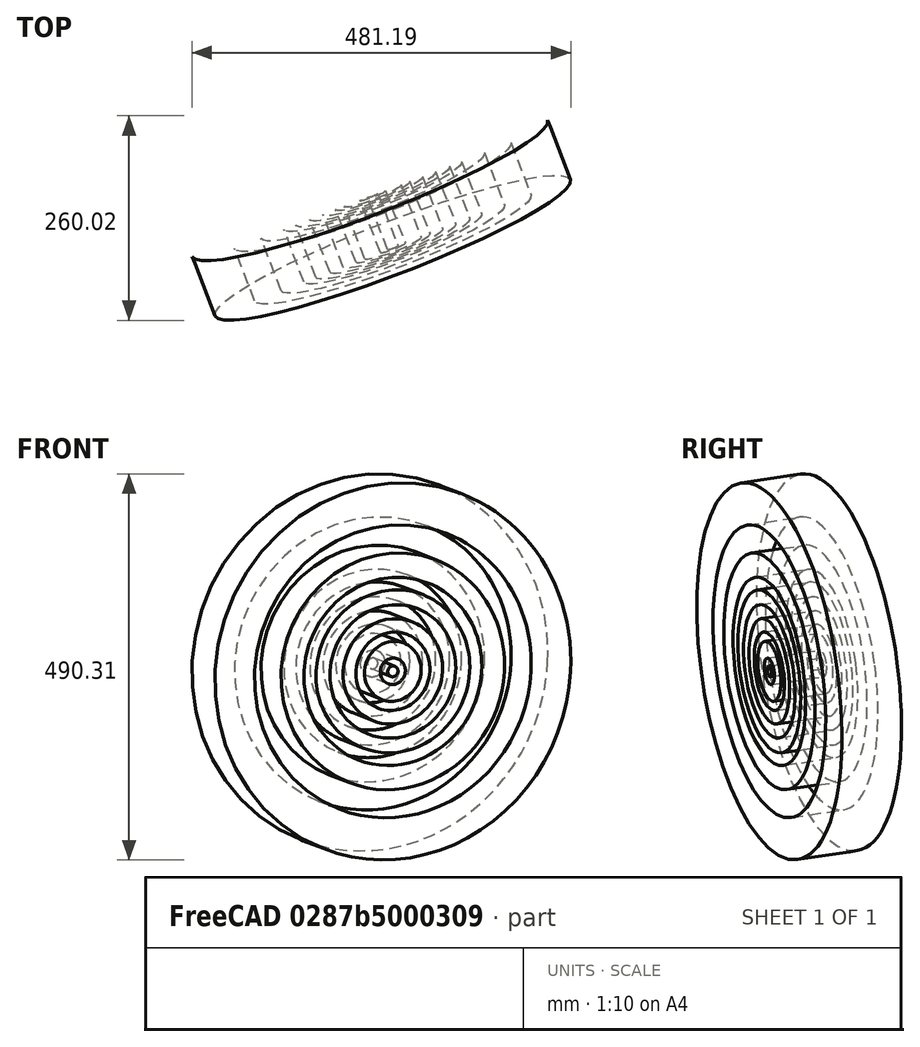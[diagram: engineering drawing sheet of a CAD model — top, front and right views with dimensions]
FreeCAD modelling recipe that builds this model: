
FCSTD DOCUMENT  (FreeCAD 0.20R25997 (Git))
Label: wirefilter_bullseye_example
License: All rights reserved
LicenseURL: http://en.wikipedia.org/wiki/All_rights_reserved
objects: Part::FeaturePython×2, PartDesign::Pad×2, Sketcher::SketchObject×1, PartDesign::Body×1
note: 8 computed .brp shape members not serialized (recipe doc carries the construction recipe); baked Part::Feature solids carry a one-line shape summary decoded from their .brp

FEATURE [Sketcher::SketchObject] Sketch
  AttachmentOffset = pos=(0,0,0) rot=(0.352249,0.933626,-0.065286;0.391935rad)
  FullyConstrained = false
  MapMode = 5
  Placement = pos=(0,0,0) rot=(0.971145,0.179991,0.156464;1.73935rad)
  sketch-geometry (15):
    g0: Circle CenterX=0 CenterY=0 CenterZ=0 NormalX=0 NormalY=0 NormalZ=1 AngleXU=0 Radius=6.93157
    g1: Circle CenterX=0 CenterY=0 CenterZ=0 NormalX=0 NormalY=0 NormalZ=1 AngleXU=0 Radius=17.0215
    g2: Circle CenterX=0 CenterY=0 CenterZ=0 NormalX=0 NormalY=0 NormalZ=1 AngleXU=0 Radius=38.5048
    g3: Circle CenterX=0 CenterY=0 CenterZ=0 NormalX=0 NormalY=0 NormalZ=1 AngleXU=0 Radius=50.3417
    g4: Circle CenterX=0 CenterY=0 CenterZ=0 NormalX=0 NormalY=0 NormalZ=1 AngleXU=0 Radius=67.6191
    g5: Circle CenterX=0 CenterY=0 CenterZ=0 NormalX=0 NormalY=0 NormalZ=1 AngleXU=0 Radius=85.57
    g6: Circle CenterX=0 CenterY=0 CenterZ=0 NormalX=0 NormalY=0 NormalZ=1 AngleXU=0 Radius=104.602
    g7: Circle CenterX=0 CenterY=0 CenterZ=0 NormalX=0 NormalY=0 NormalZ=1 AngleXU=0 Radius=120.851
    g8: Circle CenterX=0 CenterY=0 CenterZ=0 NormalX=0 NormalY=0 NormalZ=1 AngleXU=0 Radius=151.869
    g9: Circle CenterX=0 CenterY=0 CenterZ=0 NormalX=0 NormalY=0 NormalZ=1 AngleXU=0 Radius=187.882
    g10: Circle CenterX=0 CenterY=0 CenterZ=0 NormalX=0 NormalY=0 NormalZ=1 AngleXU=0 Radius=241.809
    g11: LineSegment StartX=-153.303 StartY=49.7272 StartZ=0 EndX=171.131 EndY=49.7272 EndZ=0
    g12: LineSegment StartX=171.131 StartY=49.7272 StartZ=0 EndX=171.131 EndY=-77.5486 EndZ=0
    g13: LineSegment StartX=171.131 StartY=-77.5486 StartZ=0 EndX=-153.303 EndY=-77.5486 EndZ=0
    g14: LineSegment StartX=-153.303 StartY=-77.5486 StartZ=0 EndX=-153.303 EndY=49.7272 EndZ=0
  constraints (20):
    c: Coincident(g0,g-1)
    c: Coincident(g1,g0)
    c: Coincident(g2,g0)
    c: Coincident(g3,g0)
    c: Coincident(g4,g0)
    c: Coincident(g5,g0)
    c: Coincident(g6,g0)
    c: Coincident(g7,g0)
    c: Coincident(g8,g0)
    c: Coincident(g9,g0)
    c: Coincident(g10,g0)
    c: Coincident(g11,g12)
    c: Coincident(g12,g13)
    c: Coincident(g13,g14)
    c: Coincident(g14,g11)
    c: Horizontal(g11)
    c: Horizontal(g13)
    c: Vertical(g12)
    c: Vertical(g14)
    c: PointOnObject(g12,g9)
FEATURE [Part::FeaturePython] WireFilter  # WARN: FeaturePython — macro-defined, semantics opaque (R4)
  AttacherType = Attacher::AttachEngine3D
  ClaimChildren = true
  FaceMaker = 1
  FixNormal = false
  FollowSource = true
  Normal = (-0.35488,0.924495,0.139173)
  OffsetFill = false
  OffsetIntersection = false
  OffsetJoin = 0
  OffsetOpenResult = false
  Scale = (1,1,1)
  SelectEdges = false
  Source = -> Sketch [Edge11,Edge10,Edge9,Edge8,Edge7,Edge6,Edge5,Edge4,Edge3,Edge2,Edge1]
  UseDefault = false
  UseSelected = true
  UseSelectedEdges = false
  Version = 0.2021.10.20
  WireOrder = [1,2,3,4,5,6,7,8,9,10,11,0]
FEATURE [Part::FeaturePython] WireFilter001  # WARN: FeaturePython — macro-defined, semantics opaque (R4)
  AttacherType = Attacher::AttachEngine3D
  ClaimChildren = true
  FaceMaker = 0
  FixNormal = false
  FollowSource = true
  Normal = (-0.35488,0.924495,0.139173)
  OffsetFill = false
  OffsetIntersection = false
  OffsetJoin = 0
  OffsetOpenResult = false
  Scale = (1,1,1)
  SelectEdges = false
  Source = -> Sketch
  UseDefault = false
  UseSelected = false
  UseSelectedEdges = false
  Version = 0.2021.10.20
  WireOrder = [0,0,0,0,0,0,0,0,0,0,11,0]
FEATURE [PartDesign::Pad] Pad
  Direction = (0.35488,-0.924495,-0.139173)
  Length = 10
  Length2 = 100
  Profile = -> WireFilter001
  Reversed = true
  Type = 0
FEATURE [PartDesign::Pad] Pad001
  BaseFeature = -> Pad
  Direction = (-0.35488,0.924495,0.139173)
  Length = 10
  Length2 = 100
  Profile = -> WireFilter [Face1,Face2,Face3,Face4,Face5,Face6]
  Reversed = true
  Type = 0
  UseCustomVector = true
FEATURE [PartDesign::Body] Body
  Group = -> [Sketch,WireFilter,WireFilter001,Pad,Pad001]
  Origin = -> Origin
  Placement = pos=(33,0,0) rot=(0,0,1;0rad)
  Tip = -> Pad001
